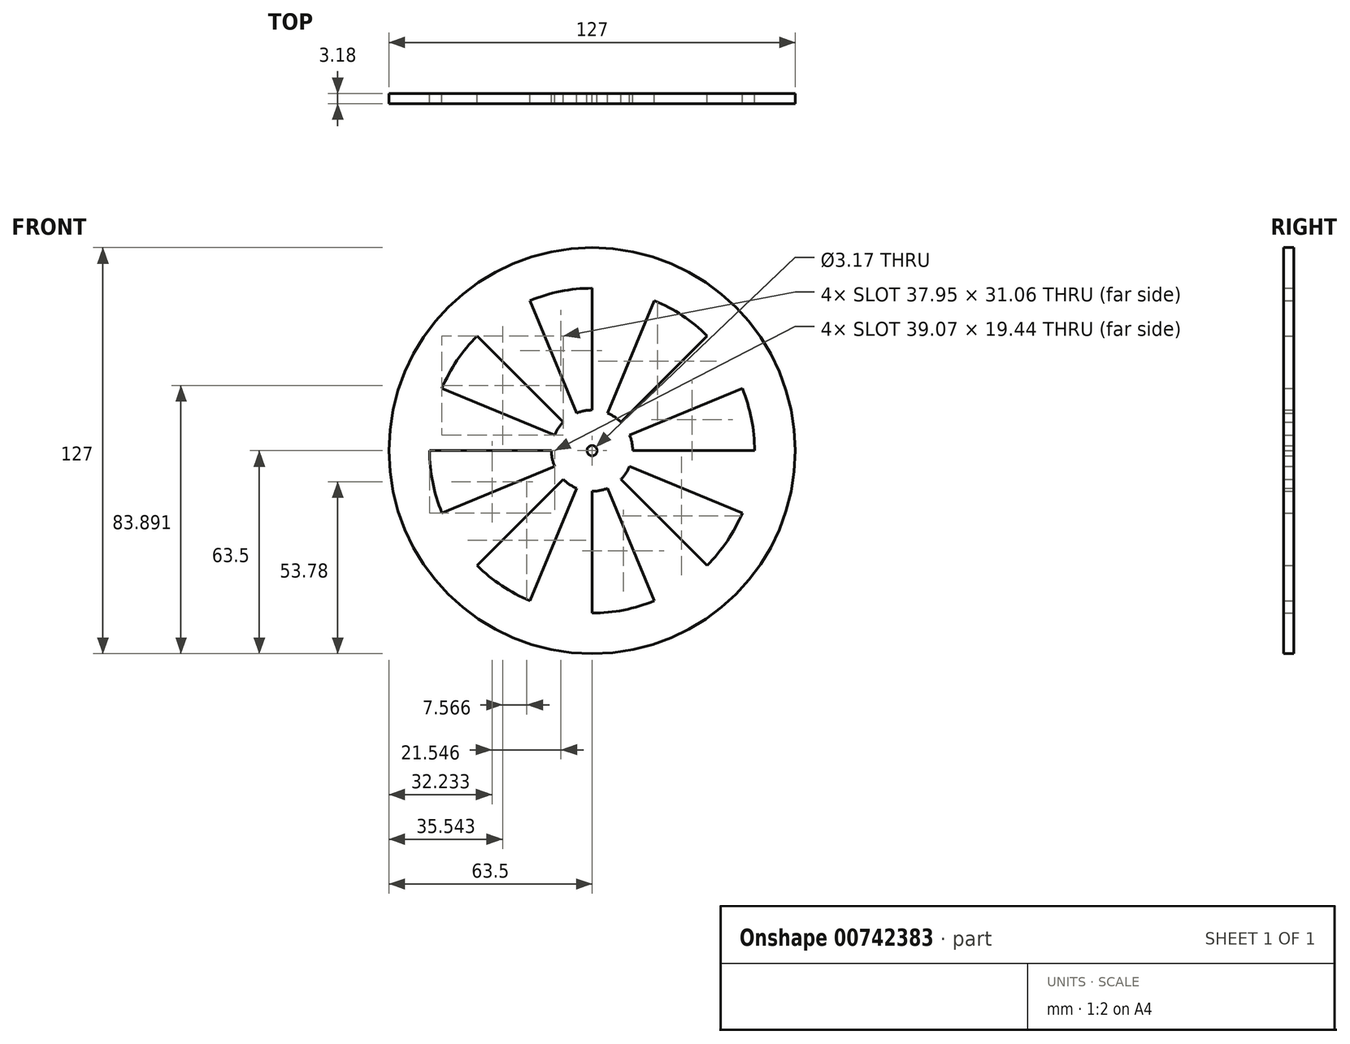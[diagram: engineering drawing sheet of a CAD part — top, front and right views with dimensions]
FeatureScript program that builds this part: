
annotation { "Feature Type Name" : "Feature", "Feature Type Description" : "" }
export const myFeature = defineFeature(function(context is Context, id is Id, definition is map)
    precondition{}
    {
        {
            var Q0;
            Q0=qCreatedBy(makeId("Front.planeOp"),FACE);
            var sketch = newSketch(context, id + "F0", { "sketchPlane" : qUnion([Q0])});
            skCircle(sketch, "E0", {"center": v(0, 0) * mm, "radius": 63.5 * mm});
            skCircle(sketch, "E1", {"center": v(0, 0) * mm, "radius": 12.7 * mm});
            skLineSegment(sketch, "E2", {"start": v(0, 63.5) * mm, "end": v(0, -63.5) * mm});
            skLineSegment(sketch, "E3", {"start": v(-63.5, 0) * mm, "end": v(63.5, 0) * mm});
            skLineSegment(sketch, "E4", {"start": v(44.9, 44.9) * mm, "end": v(0, 0) * mm});
            skLineSegment(sketch, "E5", {"start": v(0, 0) * mm, "end": v(-44.9, -44.9) * mm});
            skLineSegment(sketch, "E6", {"start": v(0, 0) * mm, "end": v(-44.9, 44.9) * mm});
            skLineSegment(sketch, "E7", {"start": v(0, 0) * mm, "end": v(44.9, -44.9) * mm});
            skLineSegment(sketch, "E8", {"start": v(-24.3, 58.67) * mm, "end": v(0, 0) * mm});
            skLineSegment(sketch, "E9", {"start": v(24.3, -58.67) * mm, "end": v(0, 0) * mm});
            skLineSegment(sketch, "E10", {"start": v(58.67, -24.3) * mm, "end": v(0, 0) * mm});
            skLineSegment(sketch, "E11", {"start": v(58.67, 24.3) * mm, "end": v(0, 0) * mm});
            skLineSegment(sketch, "E12", {"start": v(24.3, 58.67) * mm, "end": v(0, 0) * mm});
            skLineSegment(sketch, "E13", {"start": v(-58.67, 24.3) * mm, "end": v(0, 0) * mm});
            skLineSegment(sketch, "E14", {"start": v(-58.67, -24.3) * mm, "end": v(0, 0) * mm});
            skLineSegment(sketch, "E15", {"start": v(-24.3, -58.67) * mm, "end": v(0, 0) * mm});
            skCircle(sketch, "E16", {"center": v(0, 0) * mm, "radius": 50.8 * mm});
            skCircle(sketch, "E17", {"center": v(0, 0) * mm, "radius": 1.59 * mm});
            skSolve(sketch);
        }
        {
            var Q0;
            {var subQ0=sQuery(id+"F0.wireOp",EDGE,"E4");var subQ1=sQuery(id+"F0.wireOp",EDGE,"E0");var subQ2=makeQuery(id+"F0.imprint","INTERSECT",VERTEX,{"derivedFrom":[subQ1,subQ0]});Q0=makeQuery(id+"F0.imprint","IMPRINT",FACE,{"disambiguationData":[TD([[makeQuery(id+"F0.imprint","IMPRINT",EDGE,{"disambiguationData":[TD([[subQ2,-1.0]])],"derivedFrom":subQ1}),1.0]])]});}
            var Q1;
            {var subQ0=sQuery(id+"F0.wireOp",EDGE,"E2");var subQ1=sQuery(id+"F0.wireOp",EDGE,"E0");var subQ2=makeQuery(id+"F0.imprint","INTERSECT",VERTEX,{"disambiguationData":[OD(0.0)],"derivedFrom":[subQ1,subQ0]});Q1=makeQuery(id+"F0.imprint","IMPRINT",FACE,{"disambiguationData":[TD([[makeQuery(id+"F0.imprint","IMPRINT",EDGE,{"disambiguationData":[TD([[subQ2,-1.0]])],"derivedFrom":subQ1}),1.0]])]});}
            var Q2;
            {var subQ0=sQuery(id+"F0.wireOp",EDGE,"E6");var subQ1=sQuery(id+"F0.wireOp",EDGE,"E0");var subQ2=makeQuery(id+"F0.imprint","INTERSECT",VERTEX,{"derivedFrom":[subQ1,subQ0]});Q2=makeQuery(id+"F0.imprint","IMPRINT",FACE,{"disambiguationData":[TD([[makeQuery(id+"F0.imprint","IMPRINT",EDGE,{"disambiguationData":[TD([[subQ2,-1.0]])],"derivedFrom":subQ1}),1.0]])]});}
            var Q3;
            {var subQ0=sQuery(id+"F0.wireOp",EDGE,"E3");var subQ1=sQuery(id+"F0.wireOp",EDGE,"E0");var subQ2=makeQuery(id+"F0.imprint","INTERSECT",VERTEX,{"disambiguationData":[OD(0.0)],"derivedFrom":[subQ1,subQ0]});Q3=makeQuery(id+"F0.imprint","IMPRINT",FACE,{"disambiguationData":[TD([[makeQuery(id+"F0.imprint","IMPRINT",EDGE,{"disambiguationData":[TD([[subQ2,-1.0]])],"derivedFrom":subQ1}),1.0]])]});}
            var Q4;
            {var subQ0=sQuery(id+"F0.wireOp",EDGE,"E5");var subQ1=sQuery(id+"F0.wireOp",EDGE,"E0");var subQ2=makeQuery(id+"F0.imprint","INTERSECT",VERTEX,{"derivedFrom":[subQ1,subQ0]});Q4=makeQuery(id+"F0.imprint","IMPRINT",FACE,{"disambiguationData":[TD([[makeQuery(id+"F0.imprint","IMPRINT",EDGE,{"disambiguationData":[TD([[subQ2,-1.0]])],"derivedFrom":subQ1}),1.0]])]});}
            var Q5;
            {var subQ0=sQuery(id+"F0.wireOp",EDGE,"E2");var subQ1=sQuery(id+"F0.wireOp",EDGE,"E0");var subQ2=makeQuery(id+"F0.imprint","INTERSECT",VERTEX,{"disambiguationData":[OD(1.0)],"derivedFrom":[subQ1,subQ0]});Q5=makeQuery(id+"F0.imprint","IMPRINT",FACE,{"disambiguationData":[TD([[makeQuery(id+"F0.imprint","IMPRINT",EDGE,{"disambiguationData":[TD([[subQ2,-1.0]])],"derivedFrom":subQ1}),1.0]])]});}
            var Q6;
            {var subQ0=sQuery(id+"F0.wireOp",EDGE,"E7");var subQ1=sQuery(id+"F0.wireOp",EDGE,"E0");var subQ2=makeQuery(id+"F0.imprint","INTERSECT",VERTEX,{"derivedFrom":[subQ1,subQ0]});Q6=makeQuery(id+"F0.imprint","IMPRINT",FACE,{"disambiguationData":[TD([[makeQuery(id+"F0.imprint","IMPRINT",EDGE,{"disambiguationData":[TD([[subQ2,-1.0]])],"derivedFrom":subQ1}),1.0]])]});}
            var Q7;
            {var subQ0=sQuery(id+"F0.wireOp",EDGE,"E8");var subQ1=sQuery(id+"F0.wireOp",EDGE,"E1");var subQ2=makeQuery(id+"F0.imprint","INTERSECT",VERTEX,{"derivedFrom":[subQ1,subQ0]});Q7=makeQuery(id+"F0.imprint","IMPRINT",FACE,{"disambiguationData":[TD([[makeQuery(id+"F0.imprint","IMPRINT",EDGE,{"disambiguationData":[TD([[subQ2,-1.0]])],"derivedFrom":subQ1}),1.0]])]});}
            var Q8;
            {var subQ0=sQuery(id+"F0.wireOp",EDGE,"E12");var subQ1=sQuery(id+"F0.wireOp",EDGE,"E1");var subQ2=makeQuery(id+"F0.imprint","INTERSECT",VERTEX,{"derivedFrom":[subQ1,subQ0]});Q8=makeQuery(id+"F0.imprint","IMPRINT",FACE,{"disambiguationData":[TD([[makeQuery(id+"F0.imprint","IMPRINT",EDGE,{"disambiguationData":[TD([[subQ2,-1.0]])],"derivedFrom":subQ1}),1.0]])]});}
            var Q9;
            {var subQ0=sQuery(id+"F0.wireOp",EDGE,"E4");var subQ1=sQuery(id+"F0.wireOp",EDGE,"E1");var subQ2=makeQuery(id+"F0.imprint","INTERSECT",VERTEX,{"derivedFrom":[subQ1,subQ0]});Q9=makeQuery(id+"F0.imprint","IMPRINT",FACE,{"disambiguationData":[TD([[makeQuery(id+"F0.imprint","IMPRINT",EDGE,{"disambiguationData":[TD([[subQ2,-1.0]])],"derivedFrom":subQ1}),1.0]])]});}
            var Q10;
            {var subQ0=sQuery(id+"F0.wireOp",EDGE,"E11");var subQ1=sQuery(id+"F0.wireOp",EDGE,"E1");var subQ2=makeQuery(id+"F0.imprint","INTERSECT",VERTEX,{"derivedFrom":[subQ1,subQ0]});Q10=makeQuery(id+"F0.imprint","IMPRINT",FACE,{"disambiguationData":[TD([[makeQuery(id+"F0.imprint","IMPRINT",EDGE,{"disambiguationData":[TD([[subQ2,-1.0]])],"derivedFrom":subQ1}),1.0]])]});}
            var Q11;
            {var subQ0=sQuery(id+"F0.wireOp",EDGE,"E11");var subQ1=sQuery(id+"F0.wireOp",EDGE,"E1");var subQ2=makeQuery(id+"F0.imprint","INTERSECT",VERTEX,{"derivedFrom":[subQ1,subQ0]});Q11=makeQuery(id+"F0.imprint","IMPRINT",FACE,{"disambiguationData":[TD([[makeQuery(id+"F0.imprint","IMPRINT",EDGE,{"disambiguationData":[TD([[subQ2,1.0]])],"derivedFrom":subQ1}),1.0]])]});}
            var Q12;
            {var subQ0=sQuery(id+"F0.wireOp",EDGE,"E3");var subQ1=sQuery(id+"F0.wireOp",EDGE,"E1");var subQ2=makeQuery(id+"F0.imprint","INTERSECT",VERTEX,{"disambiguationData":[OD(0.0)],"derivedFrom":[subQ1,subQ0]});Q12=makeQuery(id+"F0.imprint","IMPRINT",FACE,{"disambiguationData":[TD([[makeQuery(id+"F0.imprint","IMPRINT",EDGE,{"disambiguationData":[TD([[subQ2,1.0]])],"derivedFrom":subQ1}),1.0]])]});}
            var Q13;
            {var subQ0=sQuery(id+"F0.wireOp",EDGE,"E9");var subQ1=sQuery(id+"F0.wireOp",EDGE,"E1");var subQ2=makeQuery(id+"F0.imprint","INTERSECT",VERTEX,{"derivedFrom":[subQ1,subQ0]});Q13=makeQuery(id+"F0.imprint","IMPRINT",FACE,{"disambiguationData":[TD([[makeQuery(id+"F0.imprint","IMPRINT",EDGE,{"disambiguationData":[TD([[subQ2,-1.0]])],"derivedFrom":subQ1}),1.0]])]});}
            var Q14;
            {var subQ0=sQuery(id+"F0.wireOp",EDGE,"E14");var subQ1=sQuery(id+"F0.wireOp",EDGE,"E1");var subQ2=makeQuery(id+"F0.imprint","INTERSECT",VERTEX,{"derivedFrom":[subQ1,subQ0]});Q14=makeQuery(id+"F0.imprint","IMPRINT",FACE,{"disambiguationData":[TD([[makeQuery(id+"F0.imprint","IMPRINT",EDGE,{"disambiguationData":[TD([[subQ2,-1.0]])],"derivedFrom":subQ1}),1.0]])]});}
            var Q15;
            {var subQ0=sQuery(id+"F0.wireOp",EDGE,"E13");var subQ1=sQuery(id+"F0.wireOp",EDGE,"E1");var subQ2=makeQuery(id+"F0.imprint","INTERSECT",VERTEX,{"derivedFrom":[subQ1,subQ0]});Q15=makeQuery(id+"F0.imprint","IMPRINT",FACE,{"disambiguationData":[TD([[makeQuery(id+"F0.imprint","IMPRINT",EDGE,{"disambiguationData":[TD([[subQ2,-1.0]])],"derivedFrom":subQ1}),1.0]])]});}
            var Q16;
            {var subQ0=sQuery(id+"F0.wireOp",EDGE,"E6");var subQ1=sQuery(id+"F0.wireOp",EDGE,"E1");var subQ2=makeQuery(id+"F0.imprint","INTERSECT",VERTEX,{"derivedFrom":[subQ1,subQ0]});Q16=makeQuery(id+"F0.imprint","IMPRINT",FACE,{"disambiguationData":[TD([[makeQuery(id+"F0.imprint","IMPRINT",EDGE,{"disambiguationData":[TD([[subQ2,-1.0]])],"derivedFrom":subQ1}),1.0]])]});}
            var Q17;
            {var subQ0=sQuery(id+"F0.wireOp",EDGE,"E3");var subQ1=sQuery(id+"F0.wireOp",EDGE,"E1");var subQ2=makeQuery(id+"F0.imprint","INTERSECT",VERTEX,{"disambiguationData":[OD(1.0)],"derivedFrom":[subQ1,subQ0]});Q17=makeQuery(id+"F0.imprint","IMPRINT",FACE,{"disambiguationData":[TD([[makeQuery(id+"F0.imprint","IMPRINT",EDGE,{"disambiguationData":[TD([[subQ2,-1.0]])],"derivedFrom":subQ1}),1.0]])]});}
            var Q18;
            {var subQ0=sQuery(id+"F0.wireOp",EDGE,"E5");var subQ1=sQuery(id+"F0.wireOp",EDGE,"E1");var subQ2=makeQuery(id+"F0.imprint","INTERSECT",VERTEX,{"derivedFrom":[subQ1,subQ0]});Q18=makeQuery(id+"F0.imprint","IMPRINT",FACE,{"disambiguationData":[TD([[makeQuery(id+"F0.imprint","IMPRINT",EDGE,{"disambiguationData":[TD([[subQ2,-1.0]])],"derivedFrom":subQ1}),1.0]])]});}
            var Q19;
            {var subQ0=sQuery(id+"F0.wireOp",EDGE,"E15");var subQ1=sQuery(id+"F0.wireOp",EDGE,"E1");var subQ2=makeQuery(id+"F0.imprint","INTERSECT",VERTEX,{"derivedFrom":[subQ1,subQ0]});Q19=makeQuery(id+"F0.imprint","IMPRINT",FACE,{"disambiguationData":[TD([[makeQuery(id+"F0.imprint","IMPRINT",EDGE,{"disambiguationData":[TD([[subQ2,-1.0]])],"derivedFrom":subQ1}),1.0]])]});}
            var Q20;
            {var subQ0=sQuery(id+"F0.wireOp",EDGE,"E2");var subQ1=sQuery(id+"F0.wireOp",EDGE,"E1");var subQ2=makeQuery(id+"F0.imprint","INTERSECT",VERTEX,{"disambiguationData":[OD(1.0)],"derivedFrom":[subQ1,subQ0]});Q20=makeQuery(id+"F0.imprint","IMPRINT",FACE,{"disambiguationData":[TD([[makeQuery(id+"F0.imprint","IMPRINT",EDGE,{"disambiguationData":[TD([[subQ2,-1.0]])],"derivedFrom":subQ1}),1.0]])]});}
            var Q21;
            {var subQ0=sQuery(id+"F0.wireOp",EDGE,"E7");var subQ1=sQuery(id+"F0.wireOp",EDGE,"E1");var subQ2=makeQuery(id+"F0.imprint","INTERSECT",VERTEX,{"derivedFrom":[subQ1,subQ0]});Q21=makeQuery(id+"F0.imprint","IMPRINT",FACE,{"disambiguationData":[TD([[makeQuery(id+"F0.imprint","IMPRINT",EDGE,{"disambiguationData":[TD([[subQ2,-1.0]])],"derivedFrom":subQ1}),1.0]])]});}
            var Q22;
            {var subQ0=sQuery(id+"F0.wireOp",EDGE,"E2");var subQ1=sQuery(id+"F0.wireOp",EDGE,"E1");var subQ2=makeQuery(id+"F0.imprint","INTERSECT",VERTEX,{"disambiguationData":[OD(0.0)],"derivedFrom":[subQ1,subQ0]});Q22=makeQuery(id+"F0.imprint","IMPRINT",FACE,{"disambiguationData":[TD([[makeQuery(id+"F0.imprint","IMPRINT",EDGE,{"disambiguationData":[TD([[subQ2,-1.0]])],"derivedFrom":subQ1}),1.0]])]});}
            var Q23;
            {var subQ0=sQuery(id+"F0.wireOp",EDGE,"E3");var subQ1=sQuery(id+"F0.wireOp",EDGE,"E0");var subQ2=makeQuery(id+"F0.imprint","INTERSECT",VERTEX,{"disambiguationData":[OD(1.0)],"derivedFrom":[subQ1,subQ0]});Q23=makeQuery(id+"F0.imprint","IMPRINT",FACE,{"disambiguationData":[TD([[makeQuery(id+"F0.imprint","IMPRINT",EDGE,{"disambiguationData":[TD([[subQ2,-1.0]])],"derivedFrom":subQ1}),1.0]])]});}
            var Q24;
            {var subQ0=sQuery(id+"F0.wireOp",EDGE,"E6");var subQ1=sQuery(id+"F0.wireOp",EDGE,"E0");var subQ2=makeQuery(id+"F0.imprint","INTERSECT",VERTEX,{"derivedFrom":[subQ1,subQ0]});Q24=makeQuery(id+"F0.imprint","IMPRINT",FACE,{"disambiguationData":[TD([[makeQuery(id+"F0.imprint","IMPRINT",EDGE,{"disambiguationData":[TD([[subQ2,1.0]])],"derivedFrom":subQ1}),1.0]])]});}
            var Q25;
            {var subQ0=sQuery(id+"F0.wireOp",EDGE,"E2");var subQ1=sQuery(id+"F0.wireOp",EDGE,"E0");var subQ2=makeQuery(id+"F0.imprint","INTERSECT",VERTEX,{"disambiguationData":[OD(0.0)],"derivedFrom":[subQ1,subQ0]});Q25=makeQuery(id+"F0.imprint","IMPRINT",FACE,{"disambiguationData":[TD([[makeQuery(id+"F0.imprint","IMPRINT",EDGE,{"disambiguationData":[TD([[subQ2,1.0]])],"derivedFrom":subQ1}),1.0]])]});}
            var Q26;
            {var subQ0=sQuery(id+"F0.wireOp",EDGE,"E4");var subQ1=sQuery(id+"F0.wireOp",EDGE,"E0");var subQ2=makeQuery(id+"F0.imprint","INTERSECT",VERTEX,{"derivedFrom":[subQ1,subQ0]});Q26=makeQuery(id+"F0.imprint","IMPRINT",FACE,{"disambiguationData":[TD([[makeQuery(id+"F0.imprint","IMPRINT",EDGE,{"disambiguationData":[TD([[subQ2,1.0]])],"derivedFrom":subQ1}),1.0]])]});}
            var Q27;
            {var subQ0=sQuery(id+"F0.wireOp",EDGE,"E7");var subQ1=sQuery(id+"F0.wireOp",EDGE,"E0");var subQ2=makeQuery(id+"F0.imprint","INTERSECT",VERTEX,{"derivedFrom":[subQ1,subQ0]});Q27=makeQuery(id+"F0.imprint","IMPRINT",FACE,{"disambiguationData":[TD([[makeQuery(id+"F0.imprint","IMPRINT",EDGE,{"disambiguationData":[TD([[subQ2,1.0]])],"derivedFrom":subQ1}),1.0]])]});}
            var Q28;
            {var subQ0=sQuery(id+"F0.wireOp",EDGE,"E2");var subQ1=sQuery(id+"F0.wireOp",EDGE,"E0");var subQ2=makeQuery(id+"F0.imprint","INTERSECT",VERTEX,{"disambiguationData":[OD(1.0)],"derivedFrom":[subQ1,subQ0]});Q28=makeQuery(id+"F0.imprint","IMPRINT",FACE,{"disambiguationData":[TD([[makeQuery(id+"F0.imprint","IMPRINT",EDGE,{"disambiguationData":[TD([[subQ2,1.0]])],"derivedFrom":subQ1}),1.0]])]});}
            var Q29;
            {var subQ0=sQuery(id+"F0.wireOp",EDGE,"E5");var subQ1=sQuery(id+"F0.wireOp",EDGE,"E0");var subQ2=makeQuery(id+"F0.imprint","INTERSECT",VERTEX,{"derivedFrom":[subQ1,subQ0]});Q29=makeQuery(id+"F0.imprint","IMPRINT",FACE,{"disambiguationData":[TD([[makeQuery(id+"F0.imprint","IMPRINT",EDGE,{"disambiguationData":[TD([[subQ2,1.0]])],"derivedFrom":subQ1}),1.0]])]});}
            var Q30;
            {var subQ0=sQuery(id+"F0.wireOp",EDGE,"E3");var subQ1=sQuery(id+"F0.wireOp",EDGE,"E0");var subQ2=makeQuery(id+"F0.imprint","INTERSECT",VERTEX,{"disambiguationData":[OD(0.0)],"derivedFrom":[subQ1,subQ0]});Q30=makeQuery(id+"F0.imprint","IMPRINT",FACE,{"disambiguationData":[TD([[makeQuery(id+"F0.imprint","IMPRINT",EDGE,{"disambiguationData":[TD([[subQ2,1.0]])],"derivedFrom":subQ1}),1.0]])]});}
            var Q31;
            {var subQ0=sQuery(id+"F0.wireOp",EDGE,"E13");var subQ1=sQuery(id+"F0.wireOp",EDGE,"E1");var subQ2=makeQuery(id+"F0.imprint","INTERSECT",VERTEX,{"derivedFrom":[subQ1,subQ0]});Q31=makeQuery(id+"F0.imprint","IMPRINT",FACE,{"disambiguationData":[TD([[makeQuery(id+"F0.imprint","IMPRINT",EDGE,{"disambiguationData":[TD([[subQ2,-1.0]])],"derivedFrom":subQ1}),-1.0]])]});}
            var Q32;
            {var subQ0=sQuery(id+"F0.wireOp",EDGE,"E8");var subQ1=sQuery(id+"F0.wireOp",EDGE,"E1");var subQ2=makeQuery(id+"F0.imprint","INTERSECT",VERTEX,{"derivedFrom":[subQ1,subQ0]});Q32=makeQuery(id+"F0.imprint","IMPRINT",FACE,{"disambiguationData":[TD([[makeQuery(id+"F0.imprint","IMPRINT",EDGE,{"disambiguationData":[TD([[subQ2,-1.0]])],"derivedFrom":subQ1}),-1.0]])]});}
            var Q33;
            {var subQ0=sQuery(id+"F0.wireOp",EDGE,"E12");var subQ1=sQuery(id+"F0.wireOp",EDGE,"E1");var subQ2=makeQuery(id+"F0.imprint","INTERSECT",VERTEX,{"derivedFrom":[subQ1,subQ0]});Q33=makeQuery(id+"F0.imprint","IMPRINT",FACE,{"disambiguationData":[TD([[makeQuery(id+"F0.imprint","IMPRINT",EDGE,{"disambiguationData":[TD([[subQ2,-1.0]])],"derivedFrom":subQ1}),-1.0]])]});}
            var Q34;
            {var subQ0=sQuery(id+"F0.wireOp",EDGE,"E11");var subQ1=sQuery(id+"F0.wireOp",EDGE,"E1");var subQ2=makeQuery(id+"F0.imprint","INTERSECT",VERTEX,{"derivedFrom":[subQ1,subQ0]});Q34=makeQuery(id+"F0.imprint","IMPRINT",FACE,{"disambiguationData":[TD([[makeQuery(id+"F0.imprint","IMPRINT",EDGE,{"disambiguationData":[TD([[subQ2,-1.0]])],"derivedFrom":subQ1}),-1.0]])]});}
            var Q35;
            {var subQ0=sQuery(id+"F0.wireOp",EDGE,"E3");var subQ1=sQuery(id+"F0.wireOp",EDGE,"E1");var subQ2=makeQuery(id+"F0.imprint","INTERSECT",VERTEX,{"disambiguationData":[OD(0.0)],"derivedFrom":[subQ1,subQ0]});Q35=makeQuery(id+"F0.imprint","IMPRINT",FACE,{"disambiguationData":[TD([[makeQuery(id+"F0.imprint","IMPRINT",EDGE,{"disambiguationData":[TD([[subQ2,1.0]])],"derivedFrom":subQ1}),-1.0]])]});}
            var Q36;
            {var subQ0=sQuery(id+"F0.wireOp",EDGE,"E15");var subQ1=sQuery(id+"F0.wireOp",EDGE,"E1");var subQ2=makeQuery(id+"F0.imprint","INTERSECT",VERTEX,{"derivedFrom":[subQ1,subQ0]});Q36=makeQuery(id+"F0.imprint","IMPRINT",FACE,{"disambiguationData":[TD([[makeQuery(id+"F0.imprint","IMPRINT",EDGE,{"disambiguationData":[TD([[subQ2,-1.0]])],"derivedFrom":subQ1}),-1.0]])]});}
            var Q37;
            {var subQ0=sQuery(id+"F0.wireOp",EDGE,"E14");var subQ1=sQuery(id+"F0.wireOp",EDGE,"E1");var subQ2=makeQuery(id+"F0.imprint","INTERSECT",VERTEX,{"derivedFrom":[subQ1,subQ0]});Q37=makeQuery(id+"F0.imprint","IMPRINT",FACE,{"disambiguationData":[TD([[makeQuery(id+"F0.imprint","IMPRINT",EDGE,{"disambiguationData":[TD([[subQ2,-1.0]])],"derivedFrom":subQ1}),-1.0]])]});}
            var Q38;
            {var subQ0=sQuery(id+"F0.wireOp",EDGE,"E3");var subQ1=sQuery(id+"F0.wireOp",EDGE,"E0");var subQ2=makeQuery(id+"F0.imprint","INTERSECT",VERTEX,{"disambiguationData":[OD(1.0)],"derivedFrom":[subQ1,subQ0]});Q38=makeQuery(id+"F0.imprint","IMPRINT",FACE,{"disambiguationData":[TD([[makeQuery(id+"F0.imprint","IMPRINT",EDGE,{"disambiguationData":[TD([[subQ2,1.0]])],"derivedFrom":subQ1}),1.0]])]});}
            var Q39;
            {var subQ0=sQuery(id+"F0.wireOp",EDGE,"E9");var subQ1=sQuery(id+"F0.wireOp",EDGE,"E1");var subQ2=makeQuery(id+"F0.imprint","INTERSECT",VERTEX,{"derivedFrom":[subQ1,subQ0]});Q39=makeQuery(id+"F0.imprint","IMPRINT",FACE,{"disambiguationData":[TD([[makeQuery(id+"F0.imprint","IMPRINT",EDGE,{"disambiguationData":[TD([[subQ2,-1.0]])],"derivedFrom":subQ1}),-1.0]])]});}
            extrude(context, id + "F1", {"entities" : qUnion([Q0, Q1, Q2, Q3, Q4, Q5, Q6, Q7, Q8, Q9, Q10, Q11, Q12, Q13, Q14, Q15, Q16, Q17, Q18, Q19, Q20, Q21, Q22, Q23, Q24, Q25, Q26, Q27, Q28, Q29, Q30, Q31, Q32, Q33, Q34, Q35, Q36, Q37, Q38, Q39]), "depth" : 3.17 * mm, "offsetDistance" : 25.4 * mm});
        }
    });
